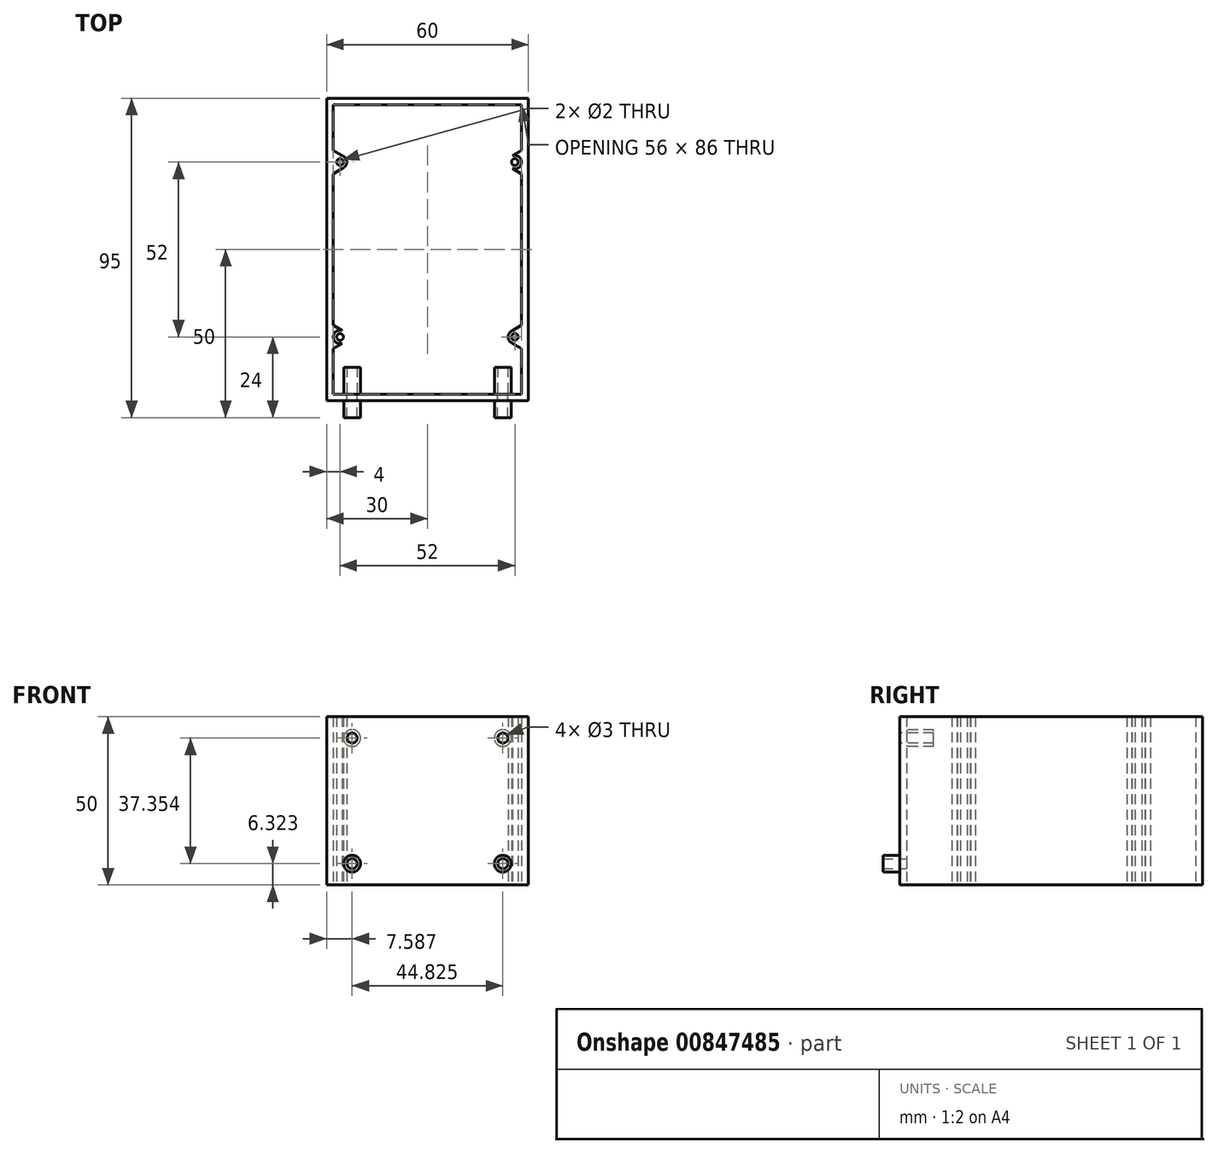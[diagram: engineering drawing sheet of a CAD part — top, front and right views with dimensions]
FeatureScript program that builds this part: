
annotation { "Feature Type Name" : "Feature", "Feature Type Description" : "" }
export const myFeature = defineFeature(function(context is Context, id is Id, definition is map)
    precondition{}
    {
        {
            var Q0;
            Q0=qCreatedBy(makeId("Top.planeOp"),FACE);
            var sketch = newSketch(context, id + "F0", { "sketchPlane" : qUnion([Q0])});
            skLineSegment(sketch, "E0.bottom", {"start": v(-30, 45) * mm, "end": v(30, 45) * mm});
            skLineSegment(sketch, "E0.top", {"start": v(-30, -45) * mm, "end": v(30, -45) * mm});
            skLineSegment(sketch, "E0.left", {"start": v(-30, 45) * mm, "end": v(-30, -45) * mm});
            skLineSegment(sketch, "E0.right", {"start": v(30, 45) * mm, "end": v(30, -45) * mm});
            skPoint(sketch, "E0.middle", {"position": v(0, 0) * mm});
            skLineSegment(sketch, "E1.bottom", {"start": v(-28, 43) * mm, "end": v(28, 43) * mm});
            skLineSegment(sketch, "E1.top", {"start": v(-28, -43) * mm, "end": v(28, -43) * mm});
            skLineSegment(sketch, "E1.left", {"start": v(-28, 43) * mm, "end": v(-28, -43) * mm});
            skLineSegment(sketch, "E1.right", {"start": v(28, 43) * mm, "end": v(28, -43) * mm});
            skCircle(sketch, "E2", {"center": v(-26, 26) * mm, "radius": 2 * mm});
            skLineSegment(sketch, "E3", {"start": v(-28, 29.5) * mm, "end": v(-24.96, 27.66) * mm});
            skLineSegment(sketch, "E4", {"start": v(-26, 26) * mm, "end": v(-28, 26) * mm, "construction": true});
            skLineSegment(sketch, "E5.MirrorCS", {"start": v(-28, 22.5) * mm, "end": v(-24.96, 24.34) * mm});
            skLineSegment(sketch, "E6.MirrorCS", {"start": v(28, 22.5) * mm, "end": v(24.96, 24.34) * mm});
            skCircle(sketch, "E7.MirrorC", {"center": v(26, 26) * mm, "radius": 2 * mm});
            skLineSegment(sketch, "E8.MirrorCS", {"start": v(28, 29.5) * mm, "end": v(24.96, 27.66) * mm});
            skLineSegment(sketch, "E9.MirrorCS", {"start": v(-28, -22.5) * mm, "end": v(-24.96, -24.34) * mm});
            skCircle(sketch, "E10.MirrorC", {"center": v(-26, -26) * mm, "radius": 2 * mm});
            skLineSegment(sketch, "E11.MirrorCS", {"start": v(-28, -29.5) * mm, "end": v(-24.96, -27.66) * mm});
            skCircle(sketch, "E12.MirrorC", {"center": v(26, -26) * mm, "radius": 2 * mm});
            skLineSegment(sketch, "E13.MirrorCS", {"start": v(28, -29.5) * mm, "end": v(24.96, -27.66) * mm});
            skLineSegment(sketch, "E14.MirrorCS", {"start": v(28, -22.5) * mm, "end": v(24.96, -24.34) * mm});
            skCircle(sketch, "E15.0", {"center": v(-26, 26) * mm, "radius": 1 * mm});
            skCircle(sketch, "E16.MirrorC", {"center": v(26, 26) * mm, "radius": 1 * mm});
            skCircle(sketch, "E17.MirrorC", {"center": v(-26, -26) * mm, "radius": 1 * mm});
            skCircle(sketch, "E18.MirrorC", {"center": v(26, -26) * mm, "radius": 1 * mm});
            skSolve(sketch);
        }
        {
            var Q0;
            Q0=makeQuery(id+"F0.imprint","IMPRINT",FACE,{"disambiguationData":[TD([[makeQuery(id+"F0.imprint","IMPRINT",EDGE,{"derivedFrom":sQuery(id+"F0.wireOp",EDGE,"E0.bottom")}),-1.0]])]});
            var Q1;
            {var subQ0=sQuery(id+"F0.wireOp",EDGE,"E9.MirrorCS");var subQ1=sQuery(id+"F0.wireOp",EDGE,"E1.left");var subQ2=makeQuery(id+"F0.imprint","INTERSECT",VERTEX,{"derivedFrom":[subQ1,subQ0]});Q1=makeQuery(id+"F0.imprint","IMPRINT",FACE,{"disambiguationData":[TD([[makeQuery(id+"F0.imprint","IMPRINT",EDGE,{"disambiguationData":[TD([[subQ2,-1.0]])],"derivedFrom":subQ1}),1.0]])]});}
            var Q2;
            Q2=makeQuery(id+"F0.imprint","IMPRINT",FACE,{"disambiguationData":[TD([[makeQuery(id+"F0.imprint","IMPRINT",EDGE,{"derivedFrom":sQuery(id+"F0.wireOp",EDGE,"E17.MirrorC")}),1.0]])]});
            var Q3;
            {var subQ0=sQuery(id+"F0.wireOp",EDGE,"E11.MirrorCS");var subQ1=sQuery(id+"F0.wireOp",EDGE,"E1.left");var subQ2=makeQuery(id+"F0.imprint","INTERSECT",VERTEX,{"derivedFrom":[subQ1,subQ0]});Q3=makeQuery(id+"F0.imprint","IMPRINT",FACE,{"disambiguationData":[TD([[makeQuery(id+"F0.imprint","IMPRINT",EDGE,{"disambiguationData":[TD([[subQ2,1.0]])],"derivedFrom":subQ1}),1.0]])]});}
            var Q4;
            {var subQ0=sQuery(id+"F0.wireOp",EDGE,"E13.MirrorCS");var subQ1=sQuery(id+"F0.wireOp",EDGE,"E1.right");var subQ2=makeQuery(id+"F0.imprint","INTERSECT",VERTEX,{"derivedFrom":[subQ1,subQ0]});Q4=makeQuery(id+"F0.imprint","IMPRINT",FACE,{"disambiguationData":[TD([[makeQuery(id+"F0.imprint","IMPRINT",EDGE,{"disambiguationData":[TD([[subQ2,1.0]])],"derivedFrom":subQ1}),-1.0]])]});}
            var Q5;
            Q5=makeQuery(id+"F0.imprint","IMPRINT",FACE,{"disambiguationData":[TD([[makeQuery(id+"F0.imprint","IMPRINT",EDGE,{"derivedFrom":sQuery(id+"F0.wireOp",EDGE,"E18.MirrorC")}),-1.0]])]});
            var Q6;
            {var subQ0=sQuery(id+"F0.wireOp",EDGE,"E14.MirrorCS");var subQ1=sQuery(id+"F0.wireOp",EDGE,"E1.right");var subQ2=makeQuery(id+"F0.imprint","INTERSECT",VERTEX,{"derivedFrom":[subQ1,subQ0]});Q6=makeQuery(id+"F0.imprint","IMPRINT",FACE,{"disambiguationData":[TD([[makeQuery(id+"F0.imprint","IMPRINT",EDGE,{"disambiguationData":[TD([[subQ2,-1.0]])],"derivedFrom":subQ1}),-1.0]])]});}
            var Q7;
            {var subQ0=sQuery(id+"F0.wireOp",EDGE,"E6.MirrorCS");var subQ1=sQuery(id+"F0.wireOp",EDGE,"E1.right");var subQ2=makeQuery(id+"F0.imprint","INTERSECT",VERTEX,{"derivedFrom":[subQ1,subQ0]});Q7=makeQuery(id+"F0.imprint","IMPRINT",FACE,{"disambiguationData":[TD([[makeQuery(id+"F0.imprint","IMPRINT",EDGE,{"disambiguationData":[TD([[subQ2,1.0]])],"derivedFrom":subQ1}),-1.0]])]});}
            var Q8;
            Q8=makeQuery(id+"F0.imprint","IMPRINT",FACE,{"disambiguationData":[TD([[makeQuery(id+"F0.imprint","IMPRINT",EDGE,{"derivedFrom":sQuery(id+"F0.wireOp",EDGE,"E16.MirrorC")}),1.0]])]});
            var Q9;
            {var subQ0=sQuery(id+"F0.wireOp",EDGE,"E8.MirrorCS");var subQ1=sQuery(id+"F0.wireOp",EDGE,"E1.right");var subQ2=makeQuery(id+"F0.imprint","INTERSECT",VERTEX,{"derivedFrom":[subQ1,subQ0]});Q9=makeQuery(id+"F0.imprint","IMPRINT",FACE,{"disambiguationData":[TD([[makeQuery(id+"F0.imprint","IMPRINT",EDGE,{"disambiguationData":[TD([[subQ2,-1.0]])],"derivedFrom":subQ1}),-1.0]])]});}
            var Q10;
            {var subQ0=sQuery(id+"F0.wireOp",EDGE,"E3");var subQ1=sQuery(id+"F0.wireOp",EDGE,"E1.left");var subQ2=makeQuery(id+"F0.imprint","INTERSECT",VERTEX,{"derivedFrom":[subQ1,subQ0]});Q10=makeQuery(id+"F0.imprint","IMPRINT",FACE,{"disambiguationData":[TD([[makeQuery(id+"F0.imprint","IMPRINT",EDGE,{"disambiguationData":[TD([[subQ2,-1.0]])],"derivedFrom":subQ1}),1.0]])]});}
            var Q11;
            Q11=makeQuery(id+"F0.imprint","IMPRINT",FACE,{"disambiguationData":[TD([[makeQuery(id+"F0.imprint","IMPRINT",EDGE,{"derivedFrom":sQuery(id+"F0.wireOp",EDGE,"E15.0")}),-1.0]])]});
            var Q12;
            {var subQ0=sQuery(id+"F0.wireOp",EDGE,"E5.MirrorCS");var subQ1=sQuery(id+"F0.wireOp",EDGE,"E1.left");var subQ2=makeQuery(id+"F0.imprint","INTERSECT",VERTEX,{"derivedFrom":[subQ1,subQ0]});Q12=makeQuery(id+"F0.imprint","IMPRINT",FACE,{"disambiguationData":[TD([[makeQuery(id+"F0.imprint","IMPRINT",EDGE,{"disambiguationData":[TD([[subQ2,1.0]])],"derivedFrom":subQ1}),1.0]])]});}
            extrude(context, id + "F1", {"entities" : qUnion([Q0, Q1, Q2, Q3, Q4, Q5, Q6, Q7, Q8, Q9, Q10, Q11, Q12]), "depth" : 50 * mm, "offsetDistance" : 25 * mm});
        }
        {
            var Q0;
            Q0=makeQuery(id+"F1.opExtrude","SWEPT_FACE",FACE,{"disambiguationData":[OSD([sQuery(id+"F0.wireOp",EDGE,"E0.top")])]});
            var sketch = newSketch(context, id + "F2", { "sketchPlane" : qUnion([Q0])});
            skLineSegment(sketch, "E19.bottom", {"start": v(-22.41, 43.68) * mm, "end": v(22.41, 43.68) * mm});
            skLineSegment(sketch, "E19.top", {"start": v(-22.41, 6.32) * mm, "end": v(22.41, 6.32) * mm});
            skLineSegment(sketch, "E19.left", {"start": v(-22.41, 43.68) * mm, "end": v(-22.41, 6.32) * mm});
            skLineSegment(sketch, "E19.right", {"start": v(22.41, 43.68) * mm, "end": v(22.41, 6.32) * mm});
            skPoint(sketch, "E19.middle", {"position": v(0, 25) * mm});
            skCircle(sketch, "E20", {"center": v(-22.41, 43.68) * mm, "radius": 1.5 * mm});
            skCircle(sketch, "E21.MirrorC", {"center": v(22.41, 43.68) * mm, "radius": 1.5 * mm});
            skCircle(sketch, "E22.0", {"center": v(-22.41, 43.68) * mm, "radius": 2.5 * mm});
            skCircle(sketch, "E23.MirrorC", {"center": v(22.41, 43.68) * mm, "radius": 2.5 * mm});
            skCircle(sketch, "E24.MirrorC", {"center": v(-22.41, 6.32) * mm, "radius": 2.5 * mm});
            skCircle(sketch, "E25.MirrorC", {"center": v(22.41, 6.32) * mm, "radius": 2.5 * mm});
            skCircle(sketch, "E26.MirrorC", {"center": v(22.41, 6.32) * mm, "radius": 1.5 * mm});
            skCircle(sketch, "E27.MirrorC", {"center": v(-22.41, 6.32) * mm, "radius": 1.5 * mm});
            skLineSegment(sketch, "E28", {"start": v(-24.91, 43.68) * mm, "end": v(-24.91, 6.32) * mm});
            skLineSegment(sketch, "E29", {"start": v(-22.41, 46.18) * mm, "end": v(22.41, 46.18) * mm});
            skLineSegment(sketch, "E30", {"start": v(0, 25) * mm, "end": v(-4.3, 25) * mm, "construction": true});
            skLineSegment(sketch, "E31.MirrorCS", {"start": v(-22.41, 3.82) * mm, "end": v(22.41, 3.82) * mm});
            skLineSegment(sketch, "E32.MirrorCS", {"start": v(24.91, 43.68) * mm, "end": v(24.91, 6.32) * mm});
            skSolve(sketch);
        }
        {
            var Q0;
            {var subQ0=sQuery(id+"F2.wireOp",EDGE,"E20");var subQ1=sQuery(id+"F2.wireOp",EDGE,"E19.bottom");var subQ2=makeQuery(id+"F2.imprint","INTERSECT",VERTEX,{"derivedFrom":[subQ1,subQ0]});Q0=makeQuery(id+"F2.imprint","IMPRINT",FACE,{"disambiguationData":[TD([[makeQuery(id+"F2.imprint","IMPRINT",EDGE,{"disambiguationData":[TD([[subQ2,-1.0]])],"derivedFrom":subQ1}),1.0]])]});}
            var Q1;
            {var subQ0=sQuery(id+"F2.wireOp",EDGE,"E20");var subQ1=sQuery(id+"F2.wireOp",EDGE,"E19.bottom");var subQ2=makeQuery(id+"F2.imprint","INTERSECT",VERTEX,{"derivedFrom":[subQ1,subQ0]});Q1=makeQuery(id+"F2.imprint","IMPRINT",FACE,{"disambiguationData":[TD([[makeQuery(id+"F2.imprint","IMPRINT",EDGE,{"disambiguationData":[TD([[subQ2,-1.0]])],"derivedFrom":subQ1}),-1.0]])]});}
            var Q2;
            {var subQ0=sQuery(id+"F2.wireOp",EDGE,"E23.MirrorC");var subQ1=sQuery(id+"F2.wireOp",EDGE,"E19.bottom");var subQ2=makeQuery(id+"F2.imprint","INTERSECT",VERTEX,{"derivedFrom":[subQ1,subQ0]});Q2=makeQuery(id+"F2.imprint","IMPRINT",FACE,{"disambiguationData":[TD([[makeQuery(id+"F2.imprint","IMPRINT",EDGE,{"disambiguationData":[TD([[subQ2,-1.0]])],"derivedFrom":subQ1}),-1.0]])]});}
            var Q3;
            {var subQ0=sQuery(id+"F2.wireOp",EDGE,"E23.MirrorC");var subQ1=sQuery(id+"F2.wireOp",EDGE,"E19.bottom");var subQ2=makeQuery(id+"F2.imprint","INTERSECT",VERTEX,{"derivedFrom":[subQ1,subQ0]});Q3=makeQuery(id+"F2.imprint","IMPRINT",FACE,{"disambiguationData":[TD([[makeQuery(id+"F2.imprint","IMPRINT",EDGE,{"disambiguationData":[TD([[subQ2,-1.0]])],"derivedFrom":subQ1}),1.0]])]});}
            extrude(context, id + "F3", {"entities" : qUnion([Q0, Q1, Q2, Q3]), "operationType" : NewBodyOperationType.ADD, "depth" : -10 * mm, "offsetDistance" : 25 * mm});
        }
        {
            var Q0;
            {var subQ0=sQuery(id+"F2.wireOp",EDGE,"E19.left");var subQ1=sQuery(id+"F2.wireOp",EDGE,"E19.bottom");var subQ2=makeQuery(id+"F2.imprint","INTERSECT",VERTEX,{"derivedFrom":[subQ1,subQ0]});Q0=makeQuery(id+"F2.imprint","IMPRINT",FACE,{"disambiguationData":[TD([[makeQuery(id+"F2.imprint","IMPRINT",EDGE,{"disambiguationData":[TD([[subQ2,-1.0]])],"derivedFrom":subQ1}),1.0]])]});}
            var Q1;
            {var subQ0=sQuery(id+"F2.wireOp",EDGE,"E19.right");var subQ1=sQuery(id+"F2.wireOp",EDGE,"E19.bottom");var subQ2=makeQuery(id+"F2.imprint","INTERSECT",VERTEX,{"derivedFrom":[subQ1,subQ0]});Q1=makeQuery(id+"F2.imprint","IMPRINT",FACE,{"disambiguationData":[TD([[makeQuery(id+"F2.imprint","IMPRINT",EDGE,{"disambiguationData":[TD([[subQ2,1.0]])],"derivedFrom":subQ1}),1.0]])]});}
            var Q2;
            {var subQ0=sQuery(id+"F2.wireOp",EDGE,"E19.right");var subQ1=sQuery(id+"F2.wireOp",EDGE,"E19.bottom");var subQ2=makeQuery(id+"F2.imprint","INTERSECT",VERTEX,{"derivedFrom":[subQ1,subQ0]});Q2=makeQuery(id+"F2.imprint","IMPRINT",FACE,{"disambiguationData":[TD([[makeQuery(id+"F2.imprint","IMPRINT",EDGE,{"disambiguationData":[TD([[subQ2,1.0]])],"derivedFrom":subQ1}),-1.0]])]});}
            var Q3;
            {var subQ0=sQuery(id+"F2.wireOp",EDGE,"E19.left");var subQ1=sQuery(id+"F2.wireOp",EDGE,"E19.bottom");var subQ2=makeQuery(id+"F2.imprint","INTERSECT",VERTEX,{"derivedFrom":[subQ1,subQ0]});Q3=makeQuery(id+"F2.imprint","IMPRINT",FACE,{"disambiguationData":[TD([[makeQuery(id+"F2.imprint","IMPRINT",EDGE,{"disambiguationData":[TD([[subQ2,-1.0]])],"derivedFrom":subQ1}),-1.0]])]});}
            extrude(context, id + "F4", {"entities" : qUnion([Q0, Q1, Q2, Q3]), "operationType" : NewBodyOperationType.REMOVE, "oppositeDirection" : true, "depth" : 25 * mm, "offsetDistance" : 25 * mm});
        }
        {
            var Q0;
            {var subQ0=sQuery(id+"F2.wireOp",EDGE,"E27.MirrorC");var subQ1=sQuery(id+"F2.wireOp",EDGE,"E19.top");var subQ2=makeQuery(id+"F2.imprint","INTERSECT",VERTEX,{"derivedFrom":[subQ1,subQ0]});Q0=makeQuery(id+"F2.imprint","IMPRINT",FACE,{"disambiguationData":[TD([[makeQuery(id+"F2.imprint","IMPRINT",EDGE,{"disambiguationData":[TD([[subQ2,-1.0]])],"derivedFrom":subQ1}),1.0]])]});}
            var Q1;
            {var subQ0=sQuery(id+"F2.wireOp",EDGE,"E27.MirrorC");var subQ1=sQuery(id+"F2.wireOp",EDGE,"E19.top");var subQ2=makeQuery(id+"F2.imprint","INTERSECT",VERTEX,{"derivedFrom":[subQ1,subQ0]});Q1=makeQuery(id+"F2.imprint","IMPRINT",FACE,{"disambiguationData":[TD([[makeQuery(id+"F2.imprint","IMPRINT",EDGE,{"disambiguationData":[TD([[subQ2,-1.0]])],"derivedFrom":subQ1}),-1.0]])]});}
            var Q2;
            {var subQ0=sQuery(id+"F2.wireOp",EDGE,"E25.MirrorC");var subQ1=sQuery(id+"F2.wireOp",EDGE,"E19.top");var subQ2=makeQuery(id+"F2.imprint","INTERSECT",VERTEX,{"derivedFrom":[subQ1,subQ0]});Q2=makeQuery(id+"F2.imprint","IMPRINT",FACE,{"disambiguationData":[TD([[makeQuery(id+"F2.imprint","IMPRINT",EDGE,{"disambiguationData":[TD([[subQ2,-1.0]])],"derivedFrom":subQ1}),1.0]])]});}
            var Q3;
            {var subQ0=sQuery(id+"F2.wireOp",EDGE,"E25.MirrorC");var subQ1=sQuery(id+"F2.wireOp",EDGE,"E19.top");var subQ2=makeQuery(id+"F2.imprint","INTERSECT",VERTEX,{"derivedFrom":[subQ1,subQ0]});Q3=makeQuery(id+"F2.imprint","IMPRINT",FACE,{"disambiguationData":[TD([[makeQuery(id+"F2.imprint","IMPRINT",EDGE,{"disambiguationData":[TD([[subQ2,-1.0]])],"derivedFrom":subQ1}),-1.0]])]});}
            extrude(context, id + "F5", {"entities" : qUnion([Q0, Q1, Q2, Q3]), "operationType" : NewBodyOperationType.ADD, "depth" : 5 * mm, "offsetDistance" : 25 * mm});
        }
        {
            var Q0;
            {var subQ0=sQuery(id+"F2.wireOp",EDGE,"E19.left");var subQ1=sQuery(id+"F2.wireOp",EDGE,"E19.top");var subQ2=makeQuery(id+"F2.imprint","INTERSECT",VERTEX,{"derivedFrom":[subQ1,subQ0]});Q0=makeQuery(id+"F2.imprint","IMPRINT",FACE,{"disambiguationData":[TD([[makeQuery(id+"F2.imprint","IMPRINT",EDGE,{"disambiguationData":[TD([[subQ2,-1.0]])],"derivedFrom":subQ1}),-1.0]])]});}
            var Q1;
            {var subQ0=sQuery(id+"F2.wireOp",EDGE,"E19.left");var subQ1=sQuery(id+"F2.wireOp",EDGE,"E19.top");var subQ2=makeQuery(id+"F2.imprint","INTERSECT",VERTEX,{"derivedFrom":[subQ1,subQ0]});Q1=makeQuery(id+"F2.imprint","IMPRINT",FACE,{"disambiguationData":[TD([[makeQuery(id+"F2.imprint","IMPRINT",EDGE,{"disambiguationData":[TD([[subQ2,-1.0]])],"derivedFrom":subQ1}),1.0]])]});}
            var Q2;
            {var subQ0=sQuery(id+"F2.wireOp",EDGE,"E19.right");var subQ1=sQuery(id+"F2.wireOp",EDGE,"E19.top");var subQ2=makeQuery(id+"F2.imprint","INTERSECT",VERTEX,{"derivedFrom":[subQ1,subQ0]});Q2=makeQuery(id+"F2.imprint","IMPRINT",FACE,{"disambiguationData":[TD([[makeQuery(id+"F2.imprint","IMPRINT",EDGE,{"disambiguationData":[TD([[subQ2,1.0]])],"derivedFrom":subQ1}),1.0]])]});}
            var Q3;
            {var subQ0=sQuery(id+"F2.wireOp",EDGE,"E19.right");var subQ1=sQuery(id+"F2.wireOp",EDGE,"E19.top");var subQ2=makeQuery(id+"F2.imprint","INTERSECT",VERTEX,{"derivedFrom":[subQ1,subQ0]});Q3=makeQuery(id+"F2.imprint","IMPRINT",FACE,{"disambiguationData":[TD([[makeQuery(id+"F2.imprint","IMPRINT",EDGE,{"disambiguationData":[TD([[subQ2,1.0]])],"derivedFrom":subQ1}),-1.0]])]});}
            extrude(context, id + "F6", {"entities" : qUnion([Q0, Q1, Q2, Q3]), "operationType" : NewBodyOperationType.REMOVE, "oppositeDirection" : true, "depth" : 25 * mm, "offsetDistance" : 25 * mm});
        }
    });
